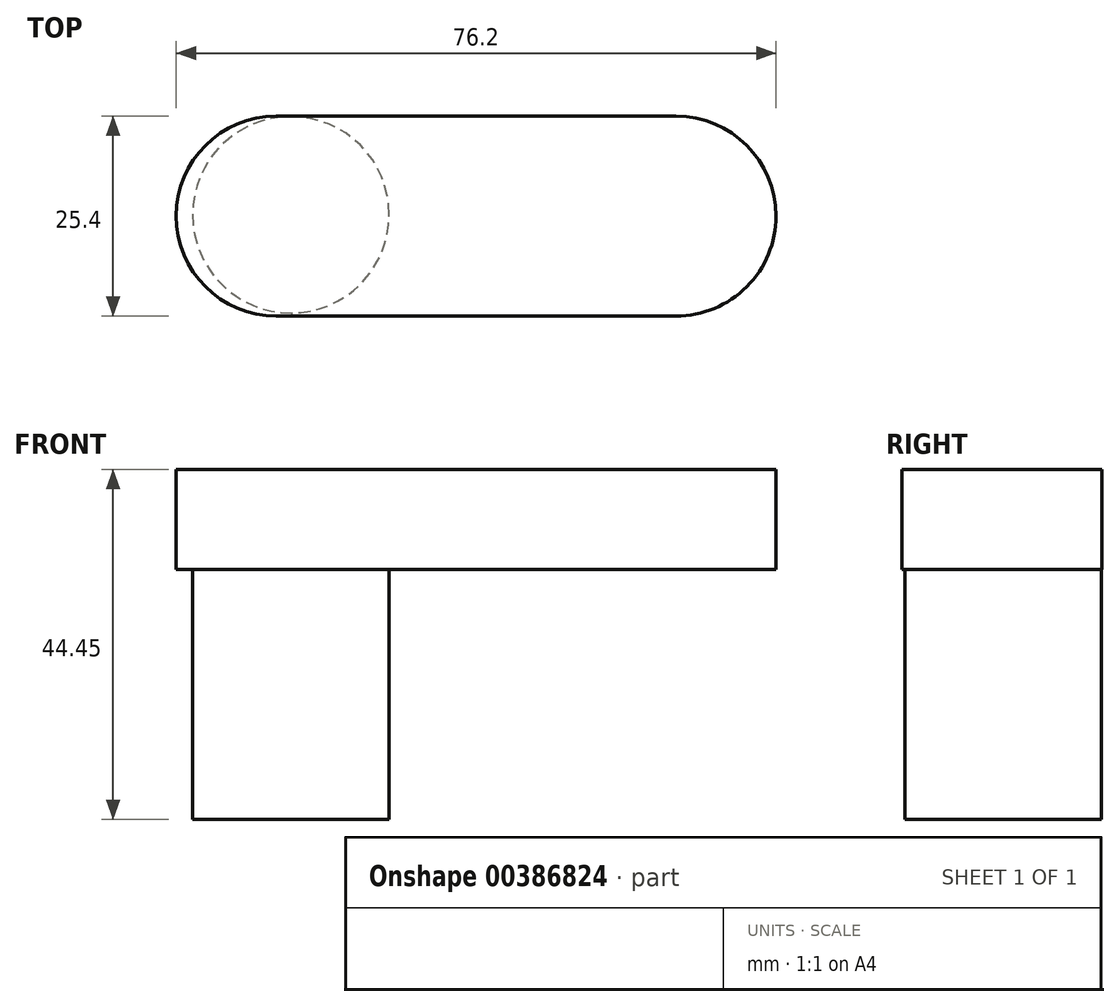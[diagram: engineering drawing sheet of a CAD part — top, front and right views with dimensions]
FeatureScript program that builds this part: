
annotation { "Feature Type Name" : "Feature", "Feature Type Description" : "" }
export const myFeature = defineFeature(function(context is Context, id is Id, definition is map)
    precondition{}
    {
        {
            var Q0;
            Q0=qCreatedBy(makeId("Top.planeOp"),FACE);
            var sketch = newSketch(context, id + "F0", { "sketchPlane" : qUnion([Q0])});
            skLineSegment(sketch, "E0", {"start": v(0, 0) * mm, "end": v(76.2, 0) * mm});
            skLineSegment(sketch, "E1", {"start": v(0, 0) * mm, "end": v(0, 25.4) * mm});
            skLineSegment(sketch, "E2", {"start": v(0, 25.4) * mm, "end": v(76.2, 25.4) * mm});
            skLineSegment(sketch, "E3", {"start": v(76.2, 25.4) * mm, "end": v(76.2, 0) * mm});
            skSolve(sketch);
        }
        {
            var Q0;
            Q0=makeQuery(id+"F0.imprint","IMPRINT",FACE,{"disambiguationData":[TD([[makeQuery(id+"F0.imprint","IMPRINT",EDGE,{"derivedFrom":sQuery(id+"F0.wireOp",EDGE,"E0")}),1.0]])]});
            extrude(context, id + "F1", {"entities" : qUnion([Q0]), "depth" : 12.7 * mm});
        }
        {
            var Q0;
            Q0=makeQuery(id+"F1.opExtrude","SWEPT_EDGE",EDGE,{"disambiguationData":[OSD([sQuery(id+"F0.wireOp",EDGE,"E2"),sQuery(id+"F0.wireOp",EDGE,"E3")])]});
            fillet(context, id + "F2", {"entities" : qUnion([Q0]), "radius" : 12.7 * mm, "tangentPropagation" : true, "allowEdgeOverflow" : false});
        }
        {
            var Q0;
            Q0=makeQuery(id+"F1.opExtrude","SWEPT_EDGE",EDGE,{"disambiguationData":[OSD([sQuery(id+"F0.wireOp",EDGE,"E0"),sQuery(id+"F0.wireOp",EDGE,"E3")])]});
            fillet(context, id + "F3", {"entities" : qUnion([Q0]), "radius" : 12.7 * mm, "tangentPropagation" : true, "allowEdgeOverflow" : false});
        }
        {
            var Q0;
            Q0=qCreatedBy(makeId("Top.planeOp"),FACE);
            var sketch = newSketch(context, id + "F4", { "sketchPlane" : qUnion([Q0])});
            skCircle(sketch, "E4", {"center": v(14.57, 12.87) * mm, "radius": 12.48 * mm});
            skSolve(sketch);
        }
        {
            var Q0;
            Q0=makeQuery(id+"F4.imprint","IMPRINT",FACE,{"disambiguationData":[TD([[makeQuery(id+"F4.imprint","IMPRINT",EDGE,{"derivedFrom":sQuery(id+"F4.wireOp",EDGE,"E4")}),1.0]])]});
            extrude(context, id + "F5", {"entities" : qUnion([Q0]), "operationType" : NewBodyOperationType.ADD, "oppositeDirection" : true, "depth" : 31.75 * mm});
        }
        {
            var Q0;
            Q0=makeQuery(id+"F5.opExtrude","CAP_FACE",FACE,{"disambiguationData":[OSD([sQuery(id+"F4.wireOp",EDGE,"E4")])],"isStart":false});
            extrude(context, id + "F6", {"entities" : qUnion([Q0]), "operationType" : NewBodyOperationType.ADD, "oppositeDirection" : true, "depth" : 12.7 * mm});
        }
        {
            var Q0;
            Q0=makeQuery(id+"F1.opExtrude","SWEPT_EDGE",EDGE,{"disambiguationData":[OSD([sQuery(id+"F0.wireOp",EDGE,"E0"),sQuery(id+"F0.wireOp",EDGE,"E1")])]});
            fillet(context, id + "F7", {"entities" : qUnion([Q0]), "radius" : 12.7 * mm, "tangentPropagation" : true, "allowEdgeOverflow" : false});
        }
        {
            var Q0;
            Q0=makeQuery(id+"F1.opExtrude","SWEPT_EDGE",EDGE,{"disambiguationData":[OSD([sQuery(id+"F0.wireOp",EDGE,"E1"),sQuery(id+"F0.wireOp",EDGE,"E2")])]});
            fillet(context, id + "F8", {"entities" : qUnion([Q0]), "radius" : 12.7 * mm, "tangentPropagation" : true, "allowEdgeOverflow" : false});
        }
        {
            var Q0;
            Q0=qCreatedBy(makeId("Top.planeOp"),FACE);
            var sketch = newSketch(context, id + "F9", { "sketchPlane" : qUnion([Q0])});
            skCircle(sketch, "E5", {"center": v(12.08, 14) * mm, "radius": 7.62 * mm});
            skSolve(sketch);
        }
        {
            var Q0;
            Q0=sQuery(id+"F9.wireOp",EDGE,"E5");
            extrude(context, id + "F10", {"bodyType" : ToolBodyType.SURFACE, "surfaceEntities" : qUnion([Q0]), "depth" : 25.4 * mm});
        }
        {
            var Q0;
            Q0=qCreatedBy(makeId("Top.planeOp"),FACE);
            var sketch = newSketch(context, id + "F11", { "sketchPlane" : qUnion([Q0])});
            skCircle(sketch, "E6", {"center": v(12.4, 13.92) * mm, "radius": 7.9 * mm});
            skSolve(sketch);
        }
        {
            var Q0;
            Q0=sQuery(id+"F11.wireOp",EDGE,"E6");
            extrude(context, id + "F12", {"bodyType" : ToolBodyType.SURFACE, "surfaceEntities" : qUnion([Q0]), "depth" : 25.4 * mm});
        }
    });
